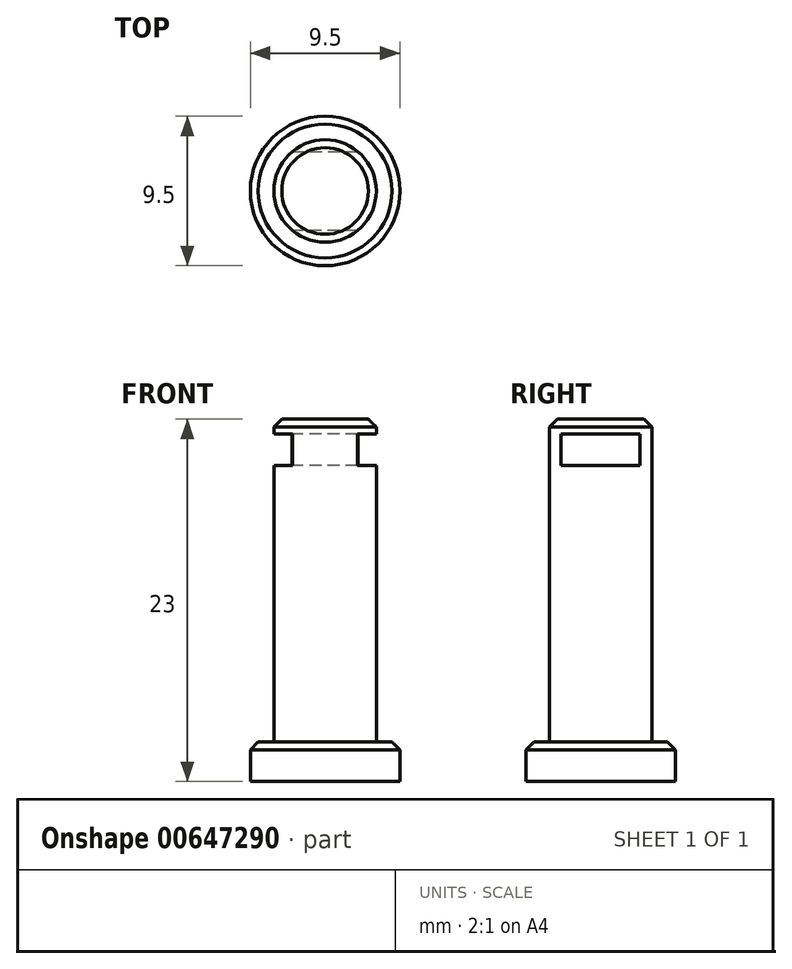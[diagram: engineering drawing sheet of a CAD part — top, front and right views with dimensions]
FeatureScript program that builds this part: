
annotation { "Feature Type Name" : "Feature", "Feature Type Description" : "" }
export const myFeature = defineFeature(function(context is Context, id is Id, definition is map)
    precondition{}
    {
        {
            var Q0;
            Q0=qCreatedBy(makeId("Top.planeOp"),FACE);
            var sketch = newSketch(context, id + "F0", { "sketchPlane" : qUnion([Q0])});
            skCircle(sketch, "E0", {"center": v(0, 0) * mm, "radius": 4.75 * mm});
            skCircle(sketch, "E1", {"center": v(0, 0) * mm, "radius": 3.25 * mm});
            skSolve(sketch);
        }
        {
            var Q0;
            Q0 = qSketchRegion(id + "F0", true);
            extrude(context, id + "F1", {"entities" : qUnion([Q0]), "depth" : 2.5 * mm, "offsetDistance" : 25.4 * mm});
        }
        {
            var Q0;
            Q0=makeQuery(id+"F0.imprint","IMPRINT",FACE,{"disambiguationData":[TD([[makeQuery(id+"F0.imprint","IMPRINT",EDGE,{"derivedFrom":sQuery(id+"F0.wireOp",EDGE,"E1")}),1.0]])]});
            extrude(context, id + "F2", {"entities" : qUnion([Q0]), "operationType" : NewBodyOperationType.ADD, "depth" : 23 * mm, "offsetDistance" : 25.4 * mm});
        }
        {
            var Q0;
            Q0=qCreatedBy(makeId("Right.planeOp"),FACE);
            var sketch = newSketch(context, id + "F3", { "sketchPlane" : qUnion([Q0])});
            skLineSegment(sketch, "E2.bottom", {"start": v(-2.51, 22.07) * mm, "end": v(2.49, 22.07) * mm});
            skLineSegment(sketch, "E2.top", {"start": v(-2.51, 20.07) * mm, "end": v(2.49, 20.07) * mm});
            skLineSegment(sketch, "E2.left", {"start": v(-2.51, 22.07) * mm, "end": v(-2.51, 20.07) * mm});
            skLineSegment(sketch, "E2.right", {"start": v(2.49, 22.07) * mm, "end": v(2.49, 20.07) * mm});
            skSolve(sketch);
        }
        {
            var Q0;
            Q0 = qSketchRegion(id + "F3", true);
            extrude(context, id + "F4", {"entities" : qUnion([Q0]), "operationType" : NewBodyOperationType.REMOVE, "endBound" : BoundingType.SYMMETRIC, "depth" : 25.4 * mm, "offsetDistance" : 25.4 * mm});
        }
        {
            var Q0;
            Q0=makeQuery(id+"F1.opExtrude","CAP_EDGE",EDGE,{"disambiguationData":[OSD([sQuery(id+"F0.wireOp",EDGE,"E0")])],"isStart":false});
            var Q1;
            Q1=makeQuery(id+"F2.opExtrude","CAP_EDGE",EDGE,{"disambiguationData":[OSD([sQuery(id+"F0.wireOp",EDGE,"E1")])],"isStart":false});
            chamfer(context, id + "F5", {"entities" : qUnion([Q0, Q1]), "width" : 0.5 * mm, "tangentPropagation" : true});
        }
    });
